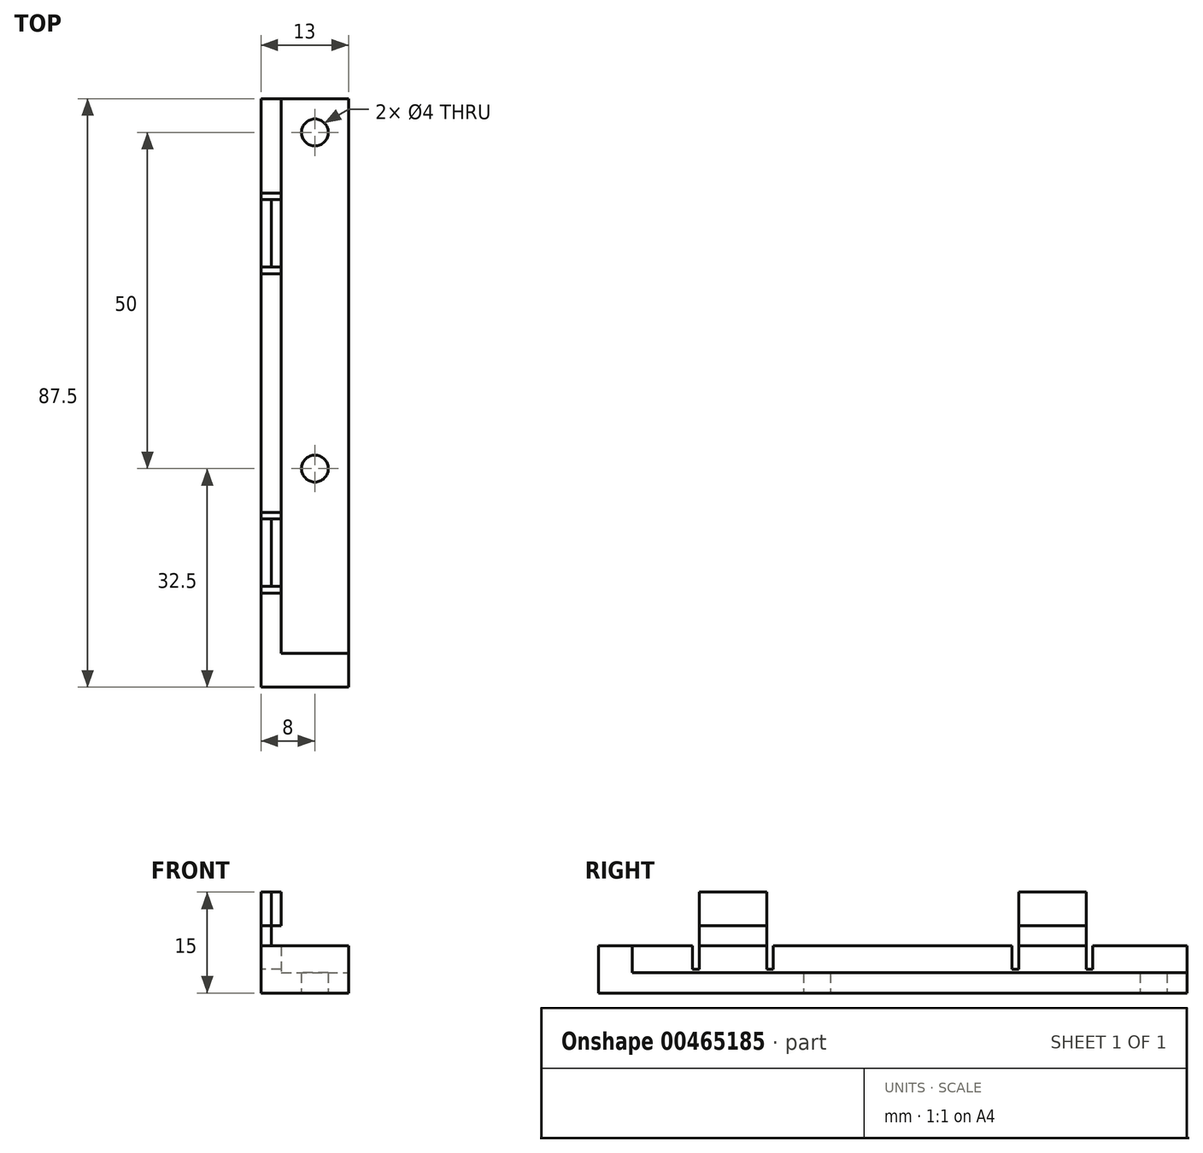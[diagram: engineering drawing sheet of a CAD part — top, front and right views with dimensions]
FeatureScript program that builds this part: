
annotation { "Feature Type Name" : "Feature", "Feature Type Description" : "" }
export const myFeature = defineFeature(function(context is Context, id is Id, definition is map)
    precondition{}
    {
        {
            var Q0;
            Q0=qCreatedBy(makeId("Top.planeOp"),FACE);
            var sketch = newSketch(context, id + "F0", { "sketchPlane" : qUnion([Q0])});
            skLineSegment(sketch, "E0.bottom", {"start": v(-113.4, 72.5) * mm, "end": v(101.6, 72.5) * mm, "construction": true});
            skLineSegment(sketch, "E0.top", {"start": v(-113.4, -42.5) * mm, "end": v(101.6, -42.5) * mm, "construction": true});
            skLineSegment(sketch, "E0.left", {"start": v(-113.4, 72.5) * mm, "end": v(-113.4, -42.5) * mm, "construction": true});
            skLineSegment(sketch, "E0.right", {"start": v(101.6, 72.5) * mm, "end": v(101.6, -42.5) * mm, "construction": true});
            skLineSegment(sketch, "E1.bottom", {"start": v(-80.9, 40) * mm, "end": v(69.1, 40) * mm, "construction": true});
            skLineSegment(sketch, "E1.top", {"start": v(-80.9, -10) * mm, "end": v(69.1, -10) * mm, "construction": true});
            skLineSegment(sketch, "E1.left", {"start": v(-80.9, 40) * mm, "end": v(-80.9, -10) * mm, "construction": true});
            skLineSegment(sketch, "E1.right", {"start": v(69.1, 40) * mm, "end": v(69.1, -10) * mm, "construction": true});
            skCircle(sketch, "E2", {"center": v(-80.9, 40) * mm, "radius": 2 * mm});
            skCircle(sketch, "E3", {"center": v(69.1, 40) * mm, "radius": 2 * mm});
            skCircle(sketch, "E4", {"center": v(69.1, -10) * mm, "radius": 2 * mm});
            skCircle(sketch, "E5", {"center": v(-80.9, -10) * mm, "radius": 2 * mm});
            skLineSegment(sketch, "E6", {"start": v(-113.4, 42.5) * mm, "end": v(101.6, 42.5) * mm, "construction": true});
            skLineSegment(sketch, "E7", {"start": v(-101.6, 42.5) * mm, "end": v(-101.6, -42.5) * mm, "construction": true});
            skLineSegment(sketch, "E8", {"start": v(-101.6, 42.5) * mm, "end": v(101.6, -42.5) * mm, "construction": true});
            skLineSegment(sketch, "E9.bottom", {"start": v(-75.9, -42.5) * mm, "end": v(-85.9, -42.5) * mm});
            skLineSegment(sketch, "E9.top", {"start": v(-75.9, 45) * mm, "end": v(-85.9, 45) * mm});
            skLineSegment(sketch, "E9.left", {"start": v(-75.9, -42.5) * mm, "end": v(-75.9, 45) * mm});
            skLineSegment(sketch, "E9.right", {"start": v(-85.9, -42.5) * mm, "end": v(-85.9, 45) * mm});
            skPoint(sketch, "E9.middle", {"position": v(-80.9, 1.25) * mm});
            skLineSegment(sketch, "E10.bottom", {"start": v(74.1, -42.5) * mm, "end": v(64.1, -42.5) * mm});
            skLineSegment(sketch, "E10.top", {"start": v(74.1, 45) * mm, "end": v(64.1, 45) * mm});
            skLineSegment(sketch, "E10.left", {"start": v(74.1, -42.5) * mm, "end": v(74.1, 45) * mm});
            skLineSegment(sketch, "E10.right", {"start": v(64.1, -42.5) * mm, "end": v(64.1, 45) * mm});
            skPoint(sketch, "E10.middle", {"position": v(69.1, 1.25) * mm});
            skLineSegment(sketch, "E11.bottom", {"start": v(-85.9, 45) * mm, "end": v(-88.9, 45) * mm});
            skLineSegment(sketch, "E11.top", {"start": v(-85.9, -42.5) * mm, "end": v(-88.9, -42.5) * mm});
            skLineSegment(sketch, "E11.left", {"start": v(-85.9, 45) * mm, "end": v(-85.9, -42.5) * mm});
            skLineSegment(sketch, "E11.right", {"start": v(-88.9, 45) * mm, "end": v(-88.9, -42.5) * mm});
            skLineSegment(sketch, "E12.bottom", {"start": v(64.1, 45) * mm, "end": v(61.1, 45) * mm});
            skLineSegment(sketch, "E12.top", {"start": v(64.1, -42.5) * mm, "end": v(61.1, -42.5) * mm});
            skLineSegment(sketch, "E12.left", {"start": v(64.1, 45) * mm, "end": v(64.1, -42.5) * mm});
            skLineSegment(sketch, "E12.right", {"start": v(61.1, 45) * mm, "end": v(61.1, -42.5) * mm});
            skLineSegment(sketch, "E13", {"start": v(-88.9, -31.5) * mm, "end": v(-85.9, -31.5) * mm});
            skLineSegment(sketch, "E14", {"start": v(-88.9, 31.5) * mm, "end": v(-85.9, 31.5) * mm});
            skLineSegment(sketch, "E15", {"start": v(61.1, 31.5) * mm, "end": v(64.1, 31.5) * mm});
            skLineSegment(sketch, "E16", {"start": v(-85.9, -37.5) * mm, "end": v(-75.9, -37.5) * mm});
            skLineSegment(sketch, "E17", {"start": v(64.1, -37.5) * mm, "end": v(74.1, -37.5) * mm});
            skLineSegment(sketch, "E18", {"start": v(61.1, -31.5) * mm, "end": v(64.1, -31.5) * mm});
            skSolve(sketch);
        }
        {
            var Q0;
            {var subQ0=sQuery(id+"F0.wireOp",EDGE,"E11.bottom");Q0=makeQuery(id+"F0.imprint","IMPRINT",FACE,{"disambiguationData":[TD([[makeQuery(id+"F0.imprint","IMPRINT",EDGE,{"derivedFrom":subQ0}),1.0]])]});}
            var Q1;
            {var subQ0=sQuery(id+"F0.wireOp",EDGE,"E13");Q1=makeQuery(id+"F0.imprint","IMPRINT",FACE,{"disambiguationData":[TD([[makeQuery(id+"F0.imprint","IMPRINT",EDGE,{"derivedFrom":subQ0}),1.0]])]});}
            var Q2;
            {var subQ1=sQuery(id+"F0.wireOp",EDGE,"E11.top");Q2=makeQuery(id+"F0.imprint","IMPRINT",FACE,{"disambiguationData":[TD([[makeQuery(id+"F0.imprint","IMPRINT",EDGE,{"derivedFrom":subQ1}),-1.0]])]});}
            var Q3;
            {var subQ0=sQuery(id+"F0.wireOp",EDGE,"E9.bottom");Q3=makeQuery(id+"F0.imprint","IMPRINT",FACE,{"disambiguationData":[TD([[makeQuery(id+"F0.imprint","IMPRINT",EDGE,{"derivedFrom":subQ0}),-1.0]])]});}
            extrude(context, id + "F1", {"entities" : qUnion([Q0, Q1, Q2, Q3]), "depth" : 7 * mm, "offsetDistance" : 25.4 * mm});
        }
        {
            var Q0;
            Q0=makeQuery(id+"F0.imprint","IMPRINT",FACE,{"disambiguationData":[TD([[makeQuery(id+"F0.imprint","IMPRINT",EDGE,{"derivedFrom":sQuery(id+"F0.wireOp",EDGE,"E2")}),-1.0]])]});
            extrude(context, id + "F2", {"entities" : qUnion([Q0]), "depth" : 3 * mm, "offsetDistance" : 25.4 * mm});
        }
        {
            var Q0;
            {var subQ0=sQuery(id+"F0.wireOp",EDGE,"E9.bottom");Q0=makeQuery(id+"F0.imprint","IMPRINT",FACE,{"disambiguationData":[TD([[makeQuery(id+"F0.imprint","IMPRINT",EDGE,{"derivedFrom":subQ0}),-1.0]])]});}
            extrude(context, id + "F3", {"entities" : qUnion([Q0]), "operationType" : NewBodyOperationType.ADD, "depth" : 3 * mm, "offsetDistance" : 25.4 * mm});
        }
        {
            var Q0;
            Q0=makeQuery(id+"F1.opExtrude","SWEPT_FACE",FACE,{"disambiguationData":[OSD([sQuery(id+"F0.wireOp",EDGE,"E11.right")])]});
            cPlane(context, id + "F4", {"entities" : qUnion([Q0]), "cplaneType" : CPlaneType.OFFSET, "offset" : 0 * mm, "width" : 152.4 * mm, "height" : 152.4 * mm});
        }
        {
            var Q0;
            Q0=qCreatedBy(id+"F4.planeOp",FACE);
            var sketch = newSketch(context, id + "F5", { "sketchPlane" : qUnion([Q0])});
            skLineSegment(sketch, "E19", {"start": v(-45, 7) * mm, "end": v(42.5, 7) * mm, "construction": true});
            skLineSegment(sketch, "E20.bottom", {"start": v(-30, 7) * mm, "end": v(-20, 7) * mm});
            skLineSegment(sketch, "E20.top", {"start": v(-30, 15) * mm, "end": v(-20, 15) * mm});
            skLineSegment(sketch, "E20.left", {"start": v(-30, 7) * mm, "end": v(-30, 15) * mm});
            skLineSegment(sketch, "E20.right", {"start": v(-20, 7) * mm, "end": v(-20, 15) * mm});
            skLineSegment(sketch, "E21.bottom", {"start": v(27.5, 7) * mm, "end": v(17.5, 7) * mm});
            skLineSegment(sketch, "E21.top", {"start": v(27.5, 15) * mm, "end": v(17.5, 15) * mm});
            skLineSegment(sketch, "E21.left", {"start": v(27.5, 7) * mm, "end": v(27.5, 15) * mm});
            skLineSegment(sketch, "E21.right", {"start": v(17.5, 7) * mm, "end": v(17.5, 15) * mm});
            skLineSegment(sketch, "E22", {"start": v(-30, 10) * mm, "end": v(-20, 10) * mm});
            skLineSegment(sketch, "E23", {"start": v(17.5, 10) * mm, "end": v(27.5, 10) * mm});
            skLineSegment(sketch, "E24.bottom", {"start": v(-30, 7) * mm, "end": v(-31, 7) * mm});
            skLineSegment(sketch, "E24.top", {"start": v(-30, 3.5) * mm, "end": v(-31, 3.5) * mm});
            skLineSegment(sketch, "E24.left", {"start": v(-30, 7) * mm, "end": v(-30, 3.5) * mm});
            skLineSegment(sketch, "E24.right", {"start": v(-31, 7) * mm, "end": v(-31, 3.5) * mm});
            skLineSegment(sketch, "E25.bottom", {"start": v(-20, 7) * mm, "end": v(-19, 7) * mm});
            skLineSegment(sketch, "E25.top", {"start": v(-20, 3.5) * mm, "end": v(-19, 3.5) * mm});
            skLineSegment(sketch, "E25.left", {"start": v(-20, 7) * mm, "end": v(-20, 3.5) * mm});
            skLineSegment(sketch, "E25.right", {"start": v(-19, 7) * mm, "end": v(-19, 3.5) * mm});
            skLineSegment(sketch, "E26.bottom", {"start": v(17.5, 7) * mm, "end": v(16.5, 7) * mm});
            skLineSegment(sketch, "E26.top", {"start": v(17.5, 3.5) * mm, "end": v(16.5, 3.5) * mm});
            skLineSegment(sketch, "E26.left", {"start": v(17.5, 7) * mm, "end": v(17.5, 3.5) * mm});
            skLineSegment(sketch, "E26.right", {"start": v(16.5, 7) * mm, "end": v(16.5, 3.5) * mm});
            skLineSegment(sketch, "E27.bottom", {"start": v(27.5, 7) * mm, "end": v(28.5, 7) * mm});
            skLineSegment(sketch, "E27.top", {"start": v(27.5, 3.5) * mm, "end": v(28.5, 3.5) * mm});
            skLineSegment(sketch, "E27.left", {"start": v(27.5, 7) * mm, "end": v(27.5, 3.5) * mm});
            skLineSegment(sketch, "E27.right", {"start": v(28.5, 7) * mm, "end": v(28.5, 3.5) * mm});
            skSolve(sketch);
        }
        {
            var Q0;
            Q0=makeQuery(id+"F5.imprint","IMPRINT",FACE,{"disambiguationData":[TD([[makeQuery(id+"F5.imprint","IMPRINT",EDGE,{"derivedFrom":sQuery(id+"F5.wireOp",EDGE,"E24.bottom")}),1.0]])]});
            var Q1;
            Q1=makeQuery(id+"F5.imprint","IMPRINT",FACE,{"disambiguationData":[TD([[makeQuery(id+"F5.imprint","IMPRINT",EDGE,{"derivedFrom":sQuery(id+"F5.wireOp",EDGE,"E25.bottom")}),-1.0]])]});
            var Q2;
            Q2=makeQuery(id+"F5.imprint","IMPRINT",FACE,{"disambiguationData":[TD([[makeQuery(id+"F5.imprint","IMPRINT",EDGE,{"derivedFrom":sQuery(id+"F5.wireOp",EDGE,"E26.bottom")}),1.0]])]});
            var Q3;
            Q3=makeQuery(id+"F5.imprint","IMPRINT",FACE,{"disambiguationData":[TD([[makeQuery(id+"F5.imprint","IMPRINT",EDGE,{"derivedFrom":sQuery(id+"F5.wireOp",EDGE,"E27.bottom")}),-1.0]])]});
            extrude(context, id + "F6", {"entities" : qUnion([Q0, Q1, Q2, Q3]), "operationType" : NewBodyOperationType.REMOVE, "endBound" : BoundingType.THROUGH_ALL, "oppositeDirection" : true, "depth" : 25.4 * mm, "offsetDistance" : 25.4 * mm});
        }
        {
            var Q0;
            {var subQ0=sQuery(id+"F5.wireOp",EDGE,"E20.top");Q0=makeQuery(id+"F5.imprint","IMPRINT",FACE,{"disambiguationData":[TD([[makeQuery(id+"F5.imprint","IMPRINT",EDGE,{"derivedFrom":subQ0}),-1.0]])]});}
            var Q1;
            {var subQ0=sQuery(id+"F5.wireOp",EDGE,"E20.bottom");Q1=makeQuery(id+"F5.imprint","IMPRINT",FACE,{"disambiguationData":[TD([[makeQuery(id+"F5.imprint","IMPRINT",EDGE,{"derivedFrom":subQ0}),1.0]])]});}
            var Q2;
            {var subQ0=sQuery(id+"F5.wireOp",EDGE,"E21.top");Q2=makeQuery(id+"F5.imprint","IMPRINT",FACE,{"disambiguationData":[TD([[makeQuery(id+"F5.imprint","IMPRINT",EDGE,{"derivedFrom":subQ0}),1.0]])]});}
            var Q3;
            {var subQ0=sQuery(id+"F5.wireOp",EDGE,"E21.bottom");Q3=makeQuery(id+"F5.imprint","IMPRINT",FACE,{"disambiguationData":[TD([[makeQuery(id+"F5.imprint","IMPRINT",EDGE,{"derivedFrom":subQ0}),-1.0]])]});}
            extrude(context, id + "F7", {"entities" : qUnion([Q0, Q1, Q2, Q3]), "oppositeDirection" : true, "depth" : 1.5 * mm, "offsetDistance" : 25.4 * mm});
        }
        {
            var Q0;
            {var subQ0=sQuery(id+"F5.wireOp",EDGE,"E21.top");Q0=makeQuery(id+"F5.imprint","IMPRINT",FACE,{"disambiguationData":[TD([[makeQuery(id+"F5.imprint","IMPRINT",EDGE,{"derivedFrom":subQ0}),1.0]])]});}
            var Q1;
            {var subQ0=sQuery(id+"F5.wireOp",EDGE,"E20.top");Q1=makeQuery(id+"F5.imprint","IMPRINT",FACE,{"disambiguationData":[TD([[makeQuery(id+"F5.imprint","IMPRINT",EDGE,{"derivedFrom":subQ0}),-1.0]])]});}
            extrude(context, id + "F8", {"entities" : qUnion([Q0, Q1]), "oppositeDirection" : true, "depth" : 3 * mm, "offsetDistance" : 25.4 * mm});
        }
    });
